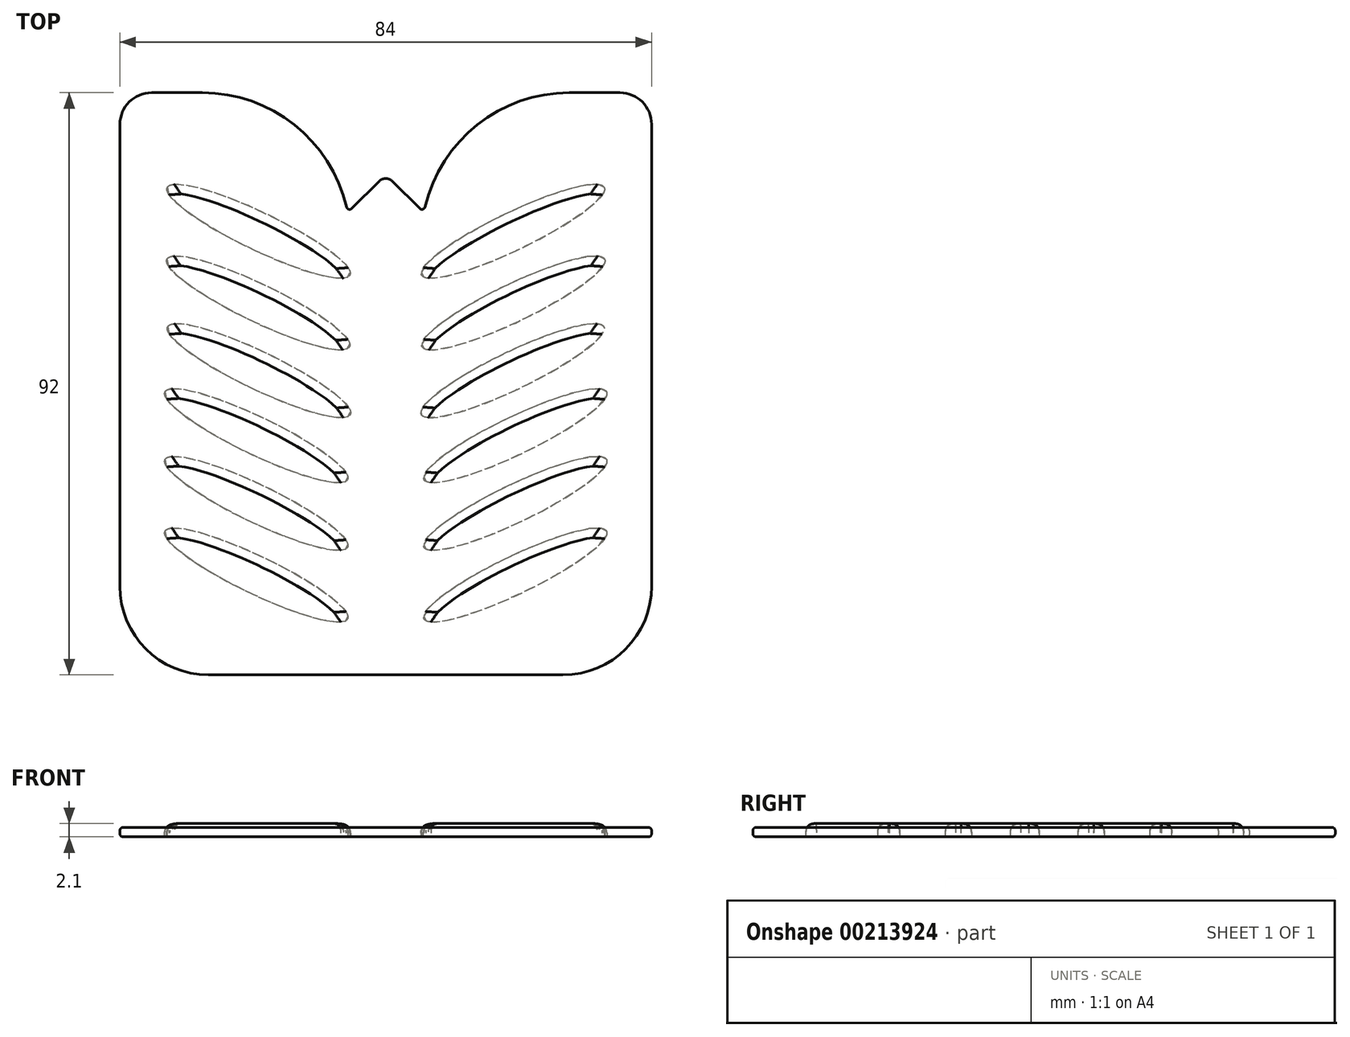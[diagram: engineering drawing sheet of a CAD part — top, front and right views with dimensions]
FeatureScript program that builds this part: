
annotation { "Feature Type Name" : "Feature", "Feature Type Description" : "" }
export const myFeature = defineFeature(function(context is Context, id is Id, definition is map)
    precondition{}
    {
        {
            var Q0;
            Q0=qCreatedBy(makeId("Top.planeOp"),FACE);
            var sketch = newSketch(context, id + "F0", { "sketchPlane" : qUnion([Q0])});
            skLineSegment(sketch, "E0", {"start": v(7.3, 45.33) * mm, "end": v(7.3, 39.33) * mm});
            skPoint(sketch, "E1.visualSharp", {"position": v(49.3, -33.73) * mm});
            skPoint(sketch, "E2.visualSharp", {"position": v(7.3, 45.33) * mm});
            skPoint(sketch, "E3.visualSharp", {"position": v(-34.7, -33.73) * mm});
            skEllipse(sketch, "E4", {"center": v(27.45, 25.04) * mm, "majorRadius": 16 * mm, "minorRadius": 3 * mm, "majorAxis": v(0.9, 0.43)});
            skEllipse(sketch, "E5", {"center": v(27.33, 14.35) * mm, "majorRadius": 16 * mm, "minorRadius": 3 * mm, "majorAxis": v(0.9, 0.43)});
            skEllipse(sketch, "E6", {"center": v(27.75, 4.07) * mm, "majorRadius": 16 * mm, "minorRadius": 3 * mm, "majorAxis": v(0.9, 0.43)});
            skEllipse(sketch, "E7", {"center": v(27.75, -6.63) * mm, "majorRadius": 16 * mm, "minorRadius": 3 * mm, "majorAxis": v(0.9, 0.43)});
            skEllipse(sketch, "E8", {"center": v(27.75, -17.95) * mm, "majorRadius": 16 * mm, "minorRadius": 3 * mm, "majorAxis": v(0.9, 0.43)});
            skEllipse(sketch, "E9.MirrorC", {"center": v(-12.85, 25.04) * mm, "majorRadius": 16 * mm, "minorRadius": 3 * mm, "majorAxis": v(-0.9, 0.43)});
            skEllipse(sketch, "E10.MirrorC", {"center": v(-12.73, 14.35) * mm, "majorRadius": 16 * mm, "minorRadius": 3 * mm, "majorAxis": v(-0.9, 0.43)});
            skEllipse(sketch, "E11.MirrorC", {"center": v(-13.15, 4.07) * mm, "majorRadius": 16 * mm, "minorRadius": 3 * mm, "majorAxis": v(-0.9, 0.43)});
            skEllipse(sketch, "E12.MirrorC", {"center": v(-13.15, -6.63) * mm, "majorRadius": 16 * mm, "minorRadius": 3 * mm, "majorAxis": v(-0.9, 0.43)});
            skEllipse(sketch, "E13.MirrorC", {"center": v(-13.15, -17.95) * mm, "majorRadius": 16 * mm, "minorRadius": 3 * mm, "majorAxis": v(-0.9, 0.43)});
            skPoint(sketch, "E14.visualSharp", {"position": v(49.3, 58.27) * mm});
            skPoint(sketch, "E15.newPointB", {"position": v(13.3, 39.33) * mm});
            skLineSegment(sketch, "E16", {"start": v(49.3, 39.27) * mm, "end": v(49.3, -19.73) * mm});
            skLineSegment(sketch, "E17", {"start": v(-20.7, -33.73) * mm, "end": v(35.3, -33.73) * mm});
            skLineSegment(sketch, "E18", {"start": v(49.3, 53.27) * mm, "end": v(49.3, 39.27) * mm});
            skLineSegment(sketch, "E19", {"start": v(44.3, 58.27) * mm, "end": v(36.3, 58.27) * mm});
            skArc(sketch, "E20.filletArc", {"start": v(49.3, 53.27) * mm, "mid": v(47.84, 56.8) * mm, "end": v(44.3, 58.27) * mm});
            skArc(sketch, "E21.filletArc", {"start": v(35.3, -33.73) * mm, "mid": v(45.2, -29.63) * mm, "end": v(49.3, -19.73) * mm});
            skLineSegment(sketch, "E22.MirrorCS", {"start": v(-29.7, 58.27) * mm, "end": v(-21.7, 58.27) * mm});
            skArc(sketch, "E23.MirrorCS", {"start": v(-34.7, 53.27) * mm, "mid": v(-33.23, 56.8) * mm, "end": v(-29.7, 58.27) * mm});
            skLineSegment(sketch, "E24.MirrorCS", {"start": v(-34.7, 53.27) * mm, "end": v(-34.7, 39.27) * mm});
            skLineSegment(sketch, "E25.MirrorCS", {"start": v(-34.7, 39.27) * mm, "end": v(-34.7, -19.73) * mm});
            skPoint(sketch, "E26.newPointA", {"position": v(-34.7, -19.73) * mm});
            skArc(sketch, "E26.filletArc", {"start": v(-34.7, -19.73) * mm, "mid": v(-30.6, -29.63) * mm, "end": v(-20.7, -33.73) * mm});
            skLineSegment(sketch, "E27", {"start": v(8.36, 44.27) * mm, "end": v(12.65, 39.98) * mm});
            skArc(sketch, "E28", {"start": v(36.3, 58.27) * mm, "mid": v(21.76, 53.21) * mm, "end": v(13.5, 40.22) * mm});
            skArc(sketch, "E29.filletArc", {"start": v(12.65, 39.98) * mm, "mid": v(13.14, 39.85) * mm, "end": v(13.5, 40.22) * mm});
            skLineSegment(sketch, "E30.MirrorCS", {"start": v(6.24, 44.27) * mm, "end": v(1.95, 39.98) * mm});
            skArc(sketch, "E31.MirrorCS", {"start": v(-21.7, 58.27) * mm, "mid": v(-7.15, 53.21) * mm, "end": v(1.11, 40.22) * mm});
            skArc(sketch, "E32.MirrorCS", {"start": v(1.95, 39.98) * mm, "mid": v(1.46, 39.85) * mm, "end": v(1.11, 40.22) * mm});
            skArc(sketch, "E33.filletArc", {"start": v(8.36, 44.27) * mm, "mid": v(7.3, 44.7) * mm, "end": v(6.24, 44.27) * mm});
            skEllipse(sketch, "E34", {"center": v(27.39, 36.37) * mm, "majorRadius": 16 * mm, "minorRadius": 3 * mm, "majorAxis": v(0.9, 0.43)});
            skEllipse(sketch, "E35.MirrorC", {"center": v(-12.78, 36.37) * mm, "majorRadius": 16 * mm, "minorRadius": 3 * mm, "majorAxis": v(-0.9, 0.43)});
            skLineSegment(sketch, "E36", {"start": v(27.33, 46.65) * mm, "end": v(27.33, 46.65) * mm});
            skSolve(sketch);
        }
        {
            var Q0;
            Q0=makeQuery(id+"F0.imprint","IMPRINT",FACE,{"disambiguationData":[TD([[makeQuery(id+"F0.imprint","IMPRINT",EDGE,{"derivedFrom":sQuery(id+"F0.wireOp",EDGE,"vnKqNRZM-WcQt-J1aC-QFi3-I3f8ndlYN3gd")}),1.0]])]});
            var Q1;
            Q1=makeQuery(id+"F0.imprint","IMPRINT",FACE,{"disambiguationData":[TD([[makeQuery(id+"F0.imprint","IMPRINT",EDGE,{"derivedFrom":sQuery(id+"F0.wireOp",EDGE,"E4")}),1.0]])]});
            var Q2;
            Q2=makeQuery(id+"F0.imprint","IMPRINT",FACE,{"disambiguationData":[TD([[makeQuery(id+"F0.imprint","IMPRINT",EDGE,{"derivedFrom":sQuery(id+"F0.wireOp",EDGE,"E5")}),1.0]])]});
            var Q3;
            Q3=makeQuery(id+"F0.imprint","IMPRINT",FACE,{"disambiguationData":[TD([[makeQuery(id+"F0.imprint","IMPRINT",EDGE,{"derivedFrom":sQuery(id+"F0.wireOp",EDGE,"E6")}),1.0]])]});
            var Q4;
            Q4=makeQuery(id+"F0.imprint","IMPRINT",FACE,{"disambiguationData":[TD([[makeQuery(id+"F0.imprint","IMPRINT",EDGE,{"derivedFrom":sQuery(id+"F0.wireOp",EDGE,"E7")}),1.0]])]});
            var Q5;
            Q5=makeQuery(id+"F0.imprint","IMPRINT",FACE,{"disambiguationData":[TD([[makeQuery(id+"F0.imprint","IMPRINT",EDGE,{"derivedFrom":sQuery(id+"F0.wireOp",EDGE,"E8")}),1.0]])]});
            var Q6;
            Q6=makeQuery(id+"F0.imprint","IMPRINT",FACE,{"disambiguationData":[TD([[makeQuery(id+"F0.imprint","IMPRINT",EDGE,{"derivedFrom":sQuery(id+"F0.wireOp",EDGE,"E13.MirrorC")}),1.0]])]});
            var Q7;
            Q7=makeQuery(id+"F0.imprint","IMPRINT",FACE,{"disambiguationData":[TD([[makeQuery(id+"F0.imprint","IMPRINT",EDGE,{"derivedFrom":sQuery(id+"F0.wireOp",EDGE,"E12.MirrorC")}),1.0]])]});
            var Q8;
            Q8=makeQuery(id+"F0.imprint","IMPRINT",FACE,{"disambiguationData":[TD([[makeQuery(id+"F0.imprint","IMPRINT",EDGE,{"derivedFrom":sQuery(id+"F0.wireOp",EDGE,"E11.MirrorC")}),1.0]])]});
            var Q9;
            Q9=makeQuery(id+"F0.imprint","IMPRINT",FACE,{"disambiguationData":[TD([[makeQuery(id+"F0.imprint","IMPRINT",EDGE,{"derivedFrom":sQuery(id+"F0.wireOp",EDGE,"E10.MirrorC")}),1.0]])]});
            var Q10;
            Q10=makeQuery(id+"F0.imprint","IMPRINT",FACE,{"disambiguationData":[TD([[makeQuery(id+"F0.imprint","IMPRINT",EDGE,{"derivedFrom":sQuery(id+"F0.wireOp",EDGE,"E9.MirrorC")}),1.0]])]});
            var Q11;
            Q11=makeQuery(id+"F0.imprint","IMPRINT",FACE,{"disambiguationData":[TD([[makeQuery(id+"F0.imprint","IMPRINT",EDGE,{"derivedFrom":sQuery(id+"F0.wireOp",EDGE,"c5122c86-c5c6-42f8-9c1e-30dec8e443cc0.MirrorC")}),1.0]])]});
            var Q12;
            Q12=makeQuery(id+"F0.imprint","IMPRINT",FACE,{"disambiguationData":[TD([[makeQuery(id+"F0.imprint","IMPRINT",EDGE,{"derivedFrom":sQuery(id+"F0.wireOp",EDGE,"E34")}),1.0]])]});
            var Q13;
            Q13=makeQuery(id+"F0.imprint","IMPRINT",FACE,{"disambiguationData":[TD([[makeQuery(id+"F0.imprint","IMPRINT",EDGE,{"derivedFrom":sQuery(id+"F0.wireOp",EDGE,"E35.MirrorC")}),1.0]])]});
            extrude(context, id + "F1", {"entities" : qUnion([Q0, Q1, Q2, Q3, Q4, Q5, Q6, Q7, Q8, Q9, Q10, Q11, Q12, Q13]), "depth" : 2.1 * mm});
        }
        {
            var Q0;
            Q0=makeQuery(id+"F1.opExtrude","CAP_EDGE",EDGE,{"disambiguationData":[OSD([sQuery(id+"F0.wireOp",EDGE,"vnKqNRZM-WcQt-J1aC-QFi3-I3f8ndlYN3gd")])],"isStart":false});
            var Q1;
            Q1=makeQuery(id+"F1.opExtrude","CAP_EDGE",EDGE,{"disambiguationData":[OSD([sQuery(id+"F0.wireOp",EDGE,"E4")])],"isStart":false});
            var Q2;
            Q2=makeQuery(id+"F1.opExtrude","CAP_EDGE",EDGE,{"disambiguationData":[OSD([sQuery(id+"F0.wireOp",EDGE,"E5")])],"isStart":false});
            var Q3;
            Q3=makeQuery(id+"F1.opExtrude","CAP_EDGE",EDGE,{"disambiguationData":[OSD([sQuery(id+"F0.wireOp",EDGE,"E6")])],"isStart":false});
            var Q4;
            Q4=makeQuery(id+"F1.opExtrude","CAP_EDGE",EDGE,{"disambiguationData":[OSD([sQuery(id+"F0.wireOp",EDGE,"E7")])],"isStart":false});
            var Q5;
            Q5=makeQuery(id+"F1.opExtrude","CAP_EDGE",EDGE,{"disambiguationData":[OSD([sQuery(id+"F0.wireOp",EDGE,"E8")])],"isStart":false});
            var Q6;
            Q6=makeQuery(id+"F1.opExtrude","CAP_EDGE",EDGE,{"disambiguationData":[OSD([sQuery(id+"F0.wireOp",EDGE,"c5122c86-c5c6-42f8-9c1e-30dec8e443cc0.MirrorC")])],"isStart":false});
            var Q7;
            Q7=makeQuery(id+"F1.opExtrude","CAP_EDGE",EDGE,{"disambiguationData":[OSD([sQuery(id+"F0.wireOp",EDGE,"E9.MirrorC")])],"isStart":false});
            var Q8;
            Q8=makeQuery(id+"F1.opExtrude","CAP_EDGE",EDGE,{"disambiguationData":[OSD([sQuery(id+"F0.wireOp",EDGE,"E10.MirrorC")])],"isStart":false});
            var Q9;
            Q9=makeQuery(id+"F1.opExtrude","CAP_EDGE",EDGE,{"disambiguationData":[OSD([sQuery(id+"F0.wireOp",EDGE,"E11.MirrorC")])],"isStart":false});
            var Q10;
            Q10=makeQuery(id+"F1.opExtrude","CAP_EDGE",EDGE,{"disambiguationData":[OSD([sQuery(id+"F0.wireOp",EDGE,"E12.MirrorC")])],"isStart":false});
            var Q11;
            Q11=makeQuery(id+"F1.opExtrude","CAP_EDGE",EDGE,{"disambiguationData":[OSD([sQuery(id+"F0.wireOp",EDGE,"E13.MirrorC")])],"isStart":false});
            var Q12;
            Q12=makeQuery(id+"F1.opExtrude","CAP_EDGE",EDGE,{"disambiguationData":[OSD([sQuery(id+"F0.wireOp",EDGE,"E34")])],"isStart":false});
            var Q13;
            Q13=makeQuery(id+"F1.opExtrude","CAP_EDGE",EDGE,{"disambiguationData":[OSD([sQuery(id+"F0.wireOp",EDGE,"E35.MirrorC")])],"isStart":false});
            fillet(context, id + "F2", {"entities" : qUnion([Q0, Q1, Q2, Q3, Q4, Q5, Q6, Q7, Q8, Q9, Q10, Q11, Q12, Q13]), "radius" : 1.5 * mm, "rho" : 0.5, "crossSection" : FilletCrossSection.CONIC, "allowEdgeOverflow" : false});
        }
        {
            var Q0;
            Q0=makeQuery(id+"F0.imprint","IMPRINT",FACE,{"disambiguationData":[TD([[makeQuery(id+"F0.imprint","IMPRINT",EDGE,{"derivedFrom":sQuery(id+"F0.wireOp",EDGE,"vnKqNRZM-WcQt-J1aC-QFi3-I3f8ndlYN3gd")}),-1.0]])]});
            var Q1;
            Q1=makeQuery(id+"F0.imprint","IMPRINT",FACE,{"disambiguationData":[TD([[makeQuery(id+"F0.imprint","IMPRINT",EDGE,{"derivedFrom":sQuery(id+"F0.wireOp",EDGE,"E8")}),1.0]])]});
            var Q2;
            Q2=makeQuery(id+"F0.imprint","IMPRINT",FACE,{"disambiguationData":[TD([[makeQuery(id+"F0.imprint","IMPRINT",EDGE,{"derivedFrom":sQuery(id+"F0.wireOp",EDGE,"E13.MirrorC")}),1.0]])]});
            var Q3;
            Q3=makeQuery(id+"F0.imprint","IMPRINT",FACE,{"disambiguationData":[TD([[makeQuery(id+"F0.imprint","IMPRINT",EDGE,{"derivedFrom":sQuery(id+"F0.wireOp",EDGE,"E12.MirrorC")}),1.0]])]});
            var Q4;
            Q4=makeQuery(id+"F0.imprint","IMPRINT",FACE,{"disambiguationData":[TD([[makeQuery(id+"F0.imprint","IMPRINT",EDGE,{"derivedFrom":sQuery(id+"F0.wireOp",EDGE,"E7")}),1.0]])]});
            var Q5;
            Q5=makeQuery(id+"F0.imprint","IMPRINT",FACE,{"disambiguationData":[TD([[makeQuery(id+"F0.imprint","IMPRINT",EDGE,{"derivedFrom":sQuery(id+"F0.wireOp",EDGE,"E6")}),1.0]])]});
            var Q6;
            Q6=makeQuery(id+"F0.imprint","IMPRINT",FACE,{"disambiguationData":[TD([[makeQuery(id+"F0.imprint","IMPRINT",EDGE,{"derivedFrom":sQuery(id+"F0.wireOp",EDGE,"E11.MirrorC")}),1.0]])]});
            var Q7;
            Q7=makeQuery(id+"F0.imprint","IMPRINT",FACE,{"disambiguationData":[TD([[makeQuery(id+"F0.imprint","IMPRINT",EDGE,{"derivedFrom":sQuery(id+"F0.wireOp",EDGE,"E10.MirrorC")}),1.0]])]});
            var Q8;
            Q8=makeQuery(id+"F0.imprint","IMPRINT",FACE,{"disambiguationData":[TD([[makeQuery(id+"F0.imprint","IMPRINT",EDGE,{"derivedFrom":sQuery(id+"F0.wireOp",EDGE,"E5")}),1.0]])]});
            var Q9;
            Q9=makeQuery(id+"F0.imprint","IMPRINT",FACE,{"disambiguationData":[TD([[makeQuery(id+"F0.imprint","IMPRINT",EDGE,{"derivedFrom":sQuery(id+"F0.wireOp",EDGE,"E9.MirrorC")}),1.0]])]});
            var Q10;
            Q10=makeQuery(id+"F0.imprint","IMPRINT",FACE,{"disambiguationData":[TD([[makeQuery(id+"F0.imprint","IMPRINT",EDGE,{"derivedFrom":sQuery(id+"F0.wireOp",EDGE,"E4")}),1.0]])]});
            var Q11;
            Q11=makeQuery(id+"F0.imprint","IMPRINT",FACE,{"disambiguationData":[TD([[makeQuery(id+"F0.imprint","IMPRINT",EDGE,{"derivedFrom":sQuery(id+"F0.wireOp",EDGE,"c5122c86-c5c6-42f8-9c1e-30dec8e443cc0.MirrorC")}),1.0]])]});
            var Q12;
            Q12=makeQuery(id+"F0.imprint","IMPRINT",FACE,{"disambiguationData":[TD([[makeQuery(id+"F0.imprint","IMPRINT",EDGE,{"derivedFrom":sQuery(id+"F0.wireOp",EDGE,"vnKqNRZM-WcQt-J1aC-QFi3-I3f8ndlYN3gd")}),1.0]])]});
            var Q13;
            Q13=makeQuery(id+"F0.imprint","IMPRINT",FACE,{"disambiguationData":[TD([[makeQuery(id+"F0.imprint","IMPRINT",EDGE,{"derivedFrom":sQuery(id+"F0.wireOp",EDGE,"E4")}),-1.0]])]});
            var Q14;
            Q14=makeQuery(id+"F0.imprint","IMPRINT",FACE,{"disambiguationData":[TD([[makeQuery(id+"F0.imprint","IMPRINT",EDGE,{"derivedFrom":sQuery(id+"F0.wireOp",EDGE,"E34")}),1.0]])]});
            var Q15;
            Q15=makeQuery(id+"F0.imprint","IMPRINT",FACE,{"disambiguationData":[TD([[makeQuery(id+"F0.imprint","IMPRINT",EDGE,{"derivedFrom":sQuery(id+"F0.wireOp",EDGE,"E35.MirrorC")}),1.0]])]});
            extrude(context, id + "F3", {"entities" : qUnion([Q0, Q1, Q2, Q3, Q4, Q5, Q6, Q7, Q8, Q9, Q10, Q11, Q12, Q13, Q14, Q15]), "depth" : 1.5 * mm});
        }
        {
            var Q0;
            Q0=makeQuery(id+"F3.opExtrude","CAP_EDGE",EDGE,{"disambiguationData":[OSD([sQuery(id+"F0.wireOp",EDGE,"E16"),sQuery(id+"F0.wireOp",EDGE,"E18")])],"isStart":false});
            var Q1;
            Q1=makeQuery(id+"F3.opExtrude","CAP_EDGE",EDGE,{"disambiguationData":[OSD([sQuery(id+"F0.wireOp",EDGE,"E17")])],"isStart":true});
            fillet(context, id + "F4", {"entities" : qUnion([Q0, Q1]), "radius" : 0.5 * mm, "tangentPropagation" : true, "allowEdgeOverflow" : false});
        }
    });
